# Revit family: IS_ConnectAir_E0824_BIM_DE
name_source: partatom
category: Plumbing Fixtures
revit_build: Autodesk Revit MEP 2014 (Build: 20130308_1515(x64)
units: mm (PartAtom-declared; Revit-internal decimal feet)

## types (6) — shared parameters
Accessories = www.idealstandard.de\ersatzteile
AreaUnits = millimeters
Assembly Code = C1030200
AssetType = Fixed
Brand = Ideal Standard
Category = FURNITURE
ConnectionType = Mechanic
Default Elevation = 800 mm  [stored 2.62467 ft]
DurationUnit = year
ExpectedLife = 25
Features = Connect Air wall mounted double vanity unit with 4 drawer
GrossWeight = 0
IfcExportAs = IfcFurnitureType
IfcExportType = FURNITURE
InstallationInstructions = www.idealstandard.de\produkte
LinearUnits = millimeters
ManufacturerURL = www.idealstandard.com
NBSDescription = Bathroom integrated furniture
NBSReference = 45-35-72/320
NettWeight = 55,6 kg
NominalHeight = 517 mm
NominalLength = 440 mm
NominalWidth = 1300 mm
ProductInformation = www.idealstandard.de/produkte
Shape = Rectangular
Size = 1300x440x517mm
Space = Internal
SpareParts = www.idealstandard.de/ersatzteile
TMV3 = No
URL = www.idealstandard.com
Uniclass2015Code = Pr_40_30_78_05
Uniclass2015Title = Bathroom integrated furniture
Uniclass2015Version = Products v1.1
Version = 1
VolumeUnits = Litres
WarrantyDescription = Manufacturers Warranty
WarrantyDurationUnit = year
zero-valued in all types: NominalDepth

## per-type parameters (varying)
| type | BIMObjectName | BarCode | Color | Description | Finish | InnerColor | MainColor | Model | ModelNumber | ModelReference | Name |
| E0824B2 - Connect Air wall mounted double vanity unit with 4 drawer(Glossy White+Matt White) | ISI_IdealStandard_BathroomIntegratedFurniture_ConnectAir_E0824B2 | 5017830519324 | Glossy White+Matt White | E0824B2 Connect Air wall mounted double vanity unit with 4 drawer | Glossy White+Matt White | ISI_IdealStandard_Laminate_White_Render | ISI_IdealStandard_Laminate_White_Render | E0824B2 | E0824B2 | E0824B2 Connect Air wall mounted double vanity unit with 4 drawer | BathroomIntegratedFurniture_ConnectAir_E0824B2_IdealStandard |
| E0824EQ - Connect Air wall mounted double vanity unit with 4 drawer(Glossy Light Grey+Matt White) | ISI_IdealStandard_BathroomIntegratedFurniture_ConnectAir_E0824EQ | 5017830519331 | Glossy Light Grey+Matt White | E0824EQ Connect Air wall mounted double vanity unit with 4 drawer | Glossy Light Grey+Matt White | ISI_IdealStandard_Laminate_White_Render | ISI_IdealStandard_Furniture_Grey_Render | E0824EQ | E0824EQ | E0824EQ Connect Air wall mounted double vanity unit with 4 drawer | BathroomIntegratedFurniture_ConnectAir_E0824EQ_IdealStandard |
| E0824KN - Connect Air wall mounted double vanity unit with 4 drawer(Glossy White+Matt Light Grey) | ISI_IdealStandard_BathroomIntegratedFurniture_ConnectAir_E0824KN | 5017830519348 | Glossy White+Matt Light Grey | E0824KN Connect Air wall mounted double vanity unit with 4 drawer | Glossy White+Matt Light Grey | ISI_IdealStandard_Furniture_Grey_Render | ISI_IdealStandard_Laminate_White_Render | E0824KN | E0824KN | E0824KN Connect Air wall mounted double vanity unit with 4 drawer | BathroomIntegratedFurniture_ConnectAir_E0824KN_IdealStandard |
| E0824PS - Connect Air wall mounted double vanity unit with 4 drawer(Wood Light Grey+Matt White) | ISI_IdealStandard_BathroomIntegratedFurniture_ConnectAir_E0824PS | 5017830519355 | Wood Light Grey+Matt White | E0824PS Connect Air wall mounted double vanity unit with 4 drawer | Wood Light Grey+Matt White | ISI_IdealStandard_Laminate_White_Render | ISI_IdealStandard_Furniture_WoodLightGrey_Render | E0824PS | E0824PS | E0824PS Connect Air wall mounted double vanity unit with 4 drawer | BathroomIntegratedFurniture_ConnectAir_E0824PS_IdealStandard |
| E0824UK - Connect Air wall mounted double vanity unit with 4 drawer(Wood Light Brown+Matt Lt Brown) | ISI_IdealStandard_BathroomIntegratedFurniture_ConnectAir_E0824UK | 5017830519362 | Wood Light Brown+Matt Lt Brown | E0824UK Connect Air wall mounted double vanity unit with 4 drawer | Wood Light Brown+Matt Lt Brown | ISI_IdealStandard__WoodLightBrown_Render | ISI_IdealStandard__WoodLightBrown_Render | E0824UK | E0824UK | E0824UK Connect Air wall mounted double vanity unit with 4 drawer | BathroomIntegratedFurniture_ConnectAir_E0824UK_IdealStandard |
| E0824VY - Connect Air wall mounted double vanity unit with 4 drawer(Matt Dark Brown+Matt White) | ISI_IdealStandard_BathroomIntegratedFurniture_ConnectAir_E0824VY | 5017830519379 | Matt Dark Brown+Matt White | E0824VY Connect Air wall mounted double vanity unit with 4 drawer | Matt Dark Brown+Matt White | ISI_IdealStandard_Laminate_White_Render | ISI_IdealStandard_Furniture_DarkBrown_Render | E0824VY | E0824VY | E0824VY Connect Air wall mounted double vanity unit with 4 drawer | BathroomIntegratedFurniture_ConnectAir_E0824VY_IdealStandard |

note: [stored X ft] marks values corroborated as IEEE doubles in the binary element streams (Revit-internal decimal feet)
